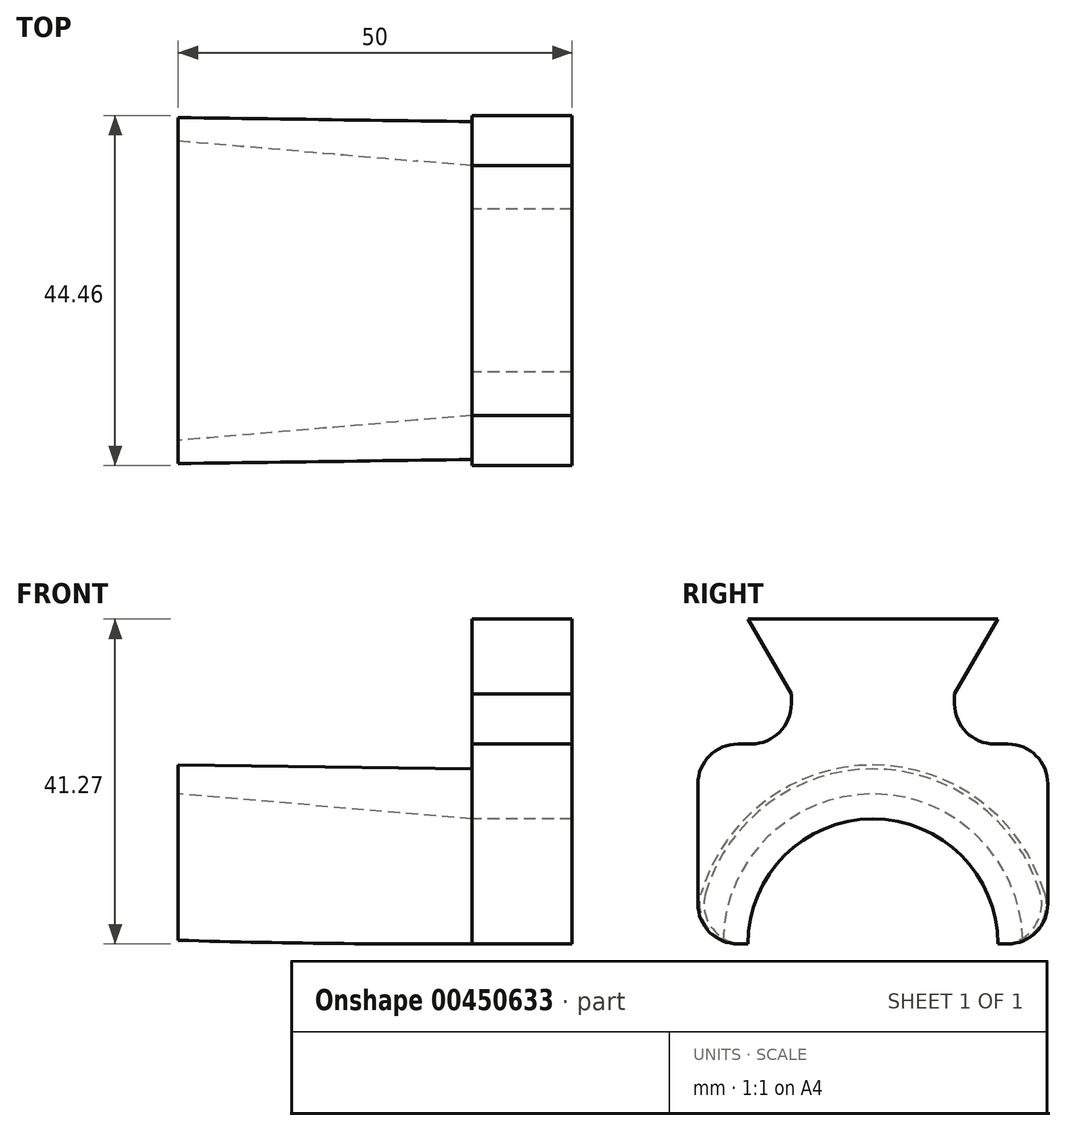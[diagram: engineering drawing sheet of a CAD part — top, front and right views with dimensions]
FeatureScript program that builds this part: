
annotation { "Feature Type Name" : "Feature", "Feature Type Description" : "" }
export const myFeature = defineFeature(function(context is Context, id is Id, definition is map)
    precondition{}
    {
        {
            var Q0;
            Q0=qCreatedBy(makeId("Right.planeOp"),FACE);
            var sketch = newSketch(context, id + "F0", { "sketchPlane" : qUnion([Q0])});
            skLineSegment(sketch, "E0", {"start": v(0, 41.28) * mm, "end": v(-15.88, 41.28) * mm});
            skLineSegment(sketch, "E1", {"start": v(-15.88, 41.28) * mm, "end": v(-10.38, 31.75) * mm});
            skArc(sketch, "E2", {"start": v(-15.88, 0) * mm, "mid": v(-11.23, 11.23) * mm, "end": v(0, 15.88) * mm});
            skLineSegment(sketch, "E3", {"start": v(-15.88, 0) * mm, "end": v(-22.23, 0) * mm});
            skLineSegment(sketch, "E4", {"start": v(-22.23, 0) * mm, "end": v(-22.23, 25.4) * mm});
            skLineSegment(sketch, "E5", {"start": v(-22.23, 25.4) * mm, "end": v(-10.38, 25.4) * mm});
            skLineSegment(sketch, "E6", {"start": v(-10.38, 25.4) * mm, "end": v(-10.38, 31.75) * mm});
            skLineSegment(sketch, "E7", {"start": v(0, 41.28) * mm, "end": v(0, 15.88) * mm});
            skSolve(sketch);
        }
        {
            var Q0;
            Q0 = qSketchRegion(id + "F0", true);
            extrude(context, id + "F1", {"entities" : qUnion([Q0]), "depth" : 12.7 * mm});
        }
        {
            var Q0;
            Q0=makeQuery(id+"F1.opExtrude","SWEPT_BODY",BODY,{"disambiguationData":[OSD([sQuery(id+"F0.wireOp",EDGE,"E0"),sQuery(id+"F0.wireOp",EDGE,"E1"),sQuery(id+"F0.wireOp",EDGE,"E2"),sQuery(id+"F0.wireOp",EDGE,"E3"),sQuery(id+"F0.wireOp",EDGE,"E4"),sQuery(id+"F0.wireOp",EDGE,"E5"),sQuery(id+"F0.wireOp",EDGE,"E6"),sQuery(id+"F0.wireOp",EDGE,"E7")])]});
            var Q1;
            Q1=qCreatedBy(makeId("Front.planeOp"),FACE);
            mirror(context, id + "F2", {"operationType" : NewBodyOperationType.ADD, "entities" : qUnion([Q0]), "mirrorPlane" : qUnion([Q1])});
        }
        {
            var Q0;
            Q0=makeQuery(id+"F1.opExtrude","SWEPT_FACE",FACE,{"disambiguationData":[OSD([sQuery(id+"F0.wireOp",EDGE,"E3")])]});
            var sketch = newSketch(context, id + "F3", { "sketchPlane" : qUnion([Q0])});
            skLineSegment(sketch, "E8", {"start": v(0, 15.88) * mm, "end": v(0, 22.23) * mm});
            skLineSegment(sketch, "E9", {"start": v(0, 22.23) * mm, "end": v(-37.3, 22.73) * mm});
            skLineSegment(sketch, "E10", {"start": v(0, 15.87) * mm, "end": v(-37.3, 19.05) * mm});
            skLineSegment(sketch, "E11", {"start": v(-37.3, 19.05) * mm, "end": v(-37.3, 22.73) * mm});
            skLineSegment(sketch, "E12", {"start": v(13.36, 0) * mm, "end": v(-18.8, 0) * mm, "construction": true});
            skSolve(sketch);
        }
        {
            var Q0;
            Q0 = qSketchRegion(id + "F3", true);
            var Q1;
            Q1=sQuery(id+"F3.wireOp",EDGE,"E12");
            revolve(context, id + "F4", {"entities" : qUnion([Q0]), "axis" : qUnion([Q1]), "revolveType" : RevolveType.ONE_DIRECTION, "angle" : 180 * degree});
        }
        {
            var Q0;
            Q0=makeQuery(id+"F1.opExtrude","SWEPT_EDGE",EDGE,{"disambiguationData":[OSD([sQuery(id+"F0.wireOp",EDGE,"E3"),sQuery(id+"F0.wireOp",EDGE,"E4")])]});
            var Q1;
            Q1=makeQuery(id+"F4.opRevolve","CAP_EDGE",EDGE,{"disambiguationData":[OSD([sQuery(id+"F3.wireOp",EDGE,"E9")])],"isStart":true});
            var Q2;
            Q2=makeQuery(id+"F1.opExtrude","SWEPT_EDGE",EDGE,{"disambiguationData":[OSD([sQuery(id+"F0.wireOp",EDGE,"E4"),sQuery(id+"F0.wireOp",EDGE,"E5")])]});
            var Q3;
            Q3=makeQuery(id+"F1.opExtrude","SWEPT_EDGE",EDGE,{"disambiguationData":[OSD([sQuery(id+"F0.wireOp",EDGE,"E5"),sQuery(id+"F0.wireOp",EDGE,"E6")])]});
            var Q4;
            Q4=makeQuery(id+"F2.opPattern","COPY",EDGE,{"derivedFrom":makeQuery(id+"F1.opExtrude","SWEPT_EDGE",EDGE,{"disambiguationData":[OSD([sQuery(id+"F0.wireOp",EDGE,"E5"),sQuery(id+"F0.wireOp",EDGE,"E6")])]}),"instanceName":"1"});
            var Q5;
            Q5=makeQuery(id+"F2.opPattern","COPY",EDGE,{"derivedFrom":makeQuery(id+"F1.opExtrude","SWEPT_EDGE",EDGE,{"disambiguationData":[OSD([sQuery(id+"F0.wireOp",EDGE,"E4"),sQuery(id+"F0.wireOp",EDGE,"E5")])]}),"instanceName":"1"});
            var Q6;
            Q6=makeQuery(id+"F4.opRevolve","CAP_EDGE",EDGE,{"disambiguationData":[OSD([sQuery(id+"F3.wireOp",EDGE,"E9")])],"isStart":false});
            var Q7;
            Q7=makeQuery(id+"F2.opPattern","COPY",EDGE,{"derivedFrom":makeQuery(id+"F1.opExtrude","SWEPT_EDGE",EDGE,{"disambiguationData":[OSD([sQuery(id+"F0.wireOp",EDGE,"E3"),sQuery(id+"F0.wireOp",EDGE,"E4")])]}),"instanceName":"1"});
            fillet(context, id + "F5", {"entities" : qUnion([Q0, Q1, Q2, Q3, Q4, Q5, Q6, Q7]), "radius" : 5.08 * mm, "tangentPropagation" : true, "allowEdgeOverflow" : false});
        }
    });
